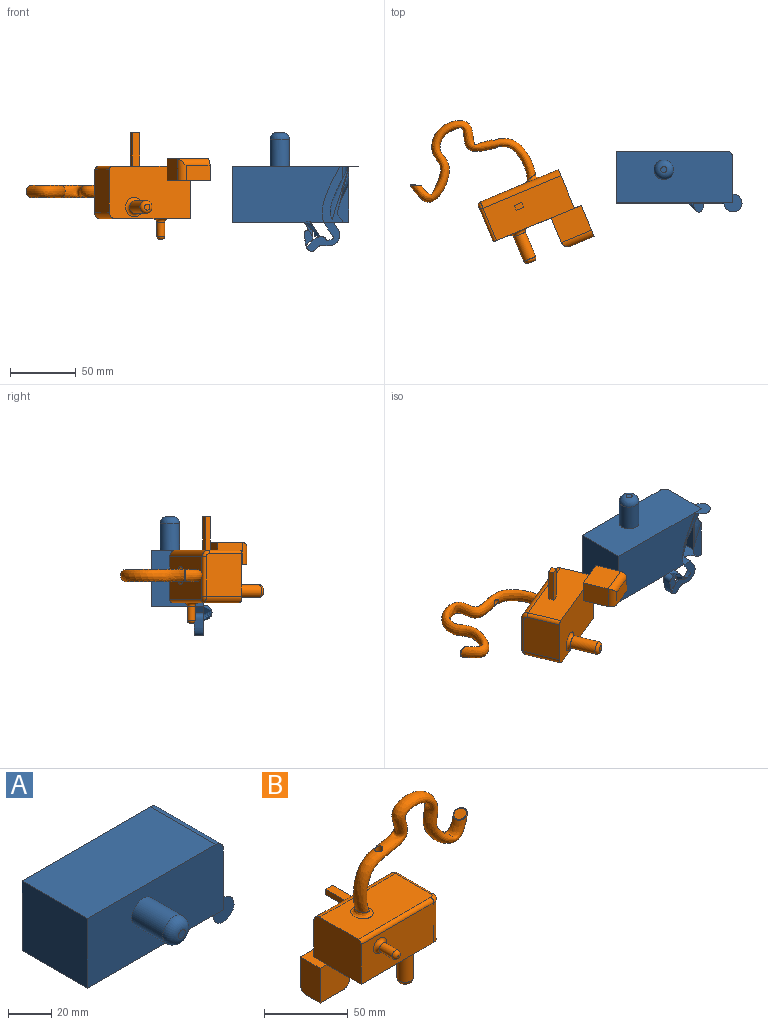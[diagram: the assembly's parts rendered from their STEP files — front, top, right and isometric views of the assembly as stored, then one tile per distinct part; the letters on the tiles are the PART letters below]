
ASSEMBLY  parts=2 mates=1
PART A: 18 faces, bbox 99x100.1x49.5 mm
  f0: plane 88.83x39.37mm, normal (0,1,0), area 3439.5mm2, adj f1,f2,f3,f5,f6,f9,f11,f13
  f1: plane 81.98x42.62mm, normal (0,0,-1), area 3046.3mm2, adj f0,f3,f4,f13,f15
  f2: plane 29.46x8.68mm, normal (0,0,-1), area 162.5mm2, adj f0,f5,f15
  f3: plane 42.61x39.37mm, normal (-1,0,0), area 1677.7mm2, adj f0,f1,f4,f6
  f4: plane 88.83x39.37mm, normal (0,-1,0), area 3320.7mm2, adj f1,f3,f5,f6,f7,f9,f12,f16
  f5: plane 42.61x34.29mm, normal (1,0,0), area 1390.4mm2, adj f0,f2,f4,f9,f15
  f6: plane 83.75x42.61mm, normal (0,0,1), area 3568.8mm2, adj f0,f3,f4,f9
  f7: cylinder r=7.38mm len=20.32mm, axis (0,1,0), area 941.7mm2, adj f4,f10
  f8: plane 4.59x4.59mm, normal (0,-1,0), area 16.6mm2, adj f10
  f9: cylinder r=5.08mm len=42.61mm, axis (0,-1,0), area 340mm2, adj f0,f4,f5,f6
  f10: torus R=2.3mm, axis (0,-1,0), area 277.2mm2, adj f7,f8
  f11: bspline ~26.97x24.13mm, area 437.2mm2, adj f0,f13,f15,f17
  f12: plane 6.86x0.02mm, normal (0,0,1), area 0.2mm2, adj f4,f14,f15,f16
  f13: plane 13.7x11.35mm, normal (0.83,-0.56,0), area 108mm2, adj f0,f1,f11,f15,f17
  f14: plane 13.7x13.7mm, normal (0,-1,0), area 110.5mm2, adj f12,f15,f16
  f15: bspline ~74.52x53.34mm, area 3313.4mm2, adj f0,f1,f2,f5,f11,f12,f13,f14
  f16: bspline ~6.85x0.79mm, area 0.2mm2, adj f4,f12,f14,f15
  f17: plane 27.14x22.5mm, normal (0,0,1), area 299.1mm2, adj f0,f11,f13,f15
PART B: 39 faces, bbox 114.5x81.1x121.9 mm
  f0: bspline ~92.41x72.32mm, area 4159.4mm2, adj f17,f26,f36
  f1: plane 64.11x26.67mm, normal (0,1,0), area 1686.8mm2, adj f2,f6,f11,f12,f13,f14,f16,f23
  f2: plane 39.99x31.75mm, normal (-1,0,0), area 1262.8mm2, adj f1,f3,f5,f6,f16,f23,f29
  f3: plane 61.57x29.21mm, normal (0,-1,0), area 1703mm2, adj f2,f6,f9,f29,f37
  f4: plane 32.37x29.21mm, normal (1,0,0), area 944.2mm2, adj f6,f9,f31,f32,f33
  f5: plane 64.11x32.37mm, normal (0,0,1), area 1935.1mm2, adj f2,f16,f29,f30,f32,f36
  f6: plane 66.65x39.99mm, normal (0,0,-1), area 2278.2mm2, adj f1,f2,f3,f4,f9,f18,f19,f31
  f7: cylinder r=2.98mm len=10.67mm, axis (0,1,0), area 199.5mm2, adj f37,f38
  f8: plane 0.87x0.87mm, normal (0,-1,0), area 0.6mm2, adj f38
  f9: cylinder r=5.08mm len=29.21mm, axis (0,0,1), area 233.1mm2, adj f3,f4,f6,f30
  f10: plane 8.18x6.77mm, normal (-0.5,0,0.87), area 49.9mm2, adj f17
  f11: plane 25.4x3.95mm, normal (1,0,0), area 100.3mm2, adj f1,f12,f14,f15
  f12: plane 25.4x5.84mm, normal (0,0,-1), area 148.4mm2, adj f1,f11,f13,f15
  f13: plane 25.4x3.95mm, normal (-1,0,0), area 100.3mm2, adj f1,f12,f14,f15
  f14: plane 25.4x5.84mm, normal (0,0,1), area 148.4mm2, adj f1,f11,f13,f15
  f15: plane 5.84x3.95mm, normal (0,1,0), area 23.1mm2, adj f11,f12,f13,f14
  f16: cylinder r=5.08mm len=64.11mm, axis (1,0,0), area 511.6mm2, adj f1,f2,f5,f33
  f17: bspline ~9.27x8.04mm, area 21.6mm2, adj f0,f10
  f18: plane 20.32x16.65mm, normal (1,0,0), area 338.3mm2, adj f6,f19,f21,f23,f28
  f19: plane 25.4x24.78mm, normal (0,-1,0), area 623.8mm2, adj f6,f18,f20,f22,f23,f28
  f20: plane 25.4x16.65mm, normal (-1,0,0), area 417.3mm2, adj f19,f21,f22,f23,f27
  f21: plane 24.78x20.32mm, normal (0,1,0), area 503.5mm2, adj f18,f20,f23,f27
  f22: plane 19.7x11.57mm, normal (0,0,-1), area 227.8mm2, adj f19,f20,f27,f28
  f23: plane 24.78x16.65mm, normal (0,0,1), area 203.2mm2, adj f1,f2,f18,f19,f20,f21
  f24: cylinder r=4.84mm len=20.07mm, axis (0,0,1), area 610.6mm2, adj f34,f35
  f25: plane 4.61x4.61mm, normal (0,0,-1), area 16.7mm2, adj f35
  f26: cylinder r=2.54mm len=7.75mm, axis (0,0,-1), area 97.8mm2, adj f0
  f27: cylinder r=5.08mm len=24.78mm, axis (-1,0,0), area 177.4mm2, adj f20,f21,f22,f28
  f28: cylinder r=5.08mm len=16.65mm, axis (0,1,0), area 112.6mm2, adj f18,f19,f22,f27
  f29: cylinder r=2.54mm len=61.57mm, axis (-1,0,0), area 245.7mm2, adj f2,f3,f5,f30
  f30: torus R=2.54mm, axis (0,0,1), area 26.1mm2, adj f5,f9,f29,f32
  f31: cylinder r=2.54mm len=26.67mm, axis (0,0,-1), area 106.4mm2, adj f1,f4,f6,f33
  f32: cylinder r=2.54mm len=29.83mm, axis (0,-1,0), area 119mm2, adj f4,f5,f30,f33
  f33: torus R=2.54mm, axis (1,0,0), area 26.1mm2, adj f4,f16,f31,f32
  f34: torus R=7.38mm, axis (0,0,1), area 144.5mm2, adj f6,f24
  f35: torus R=2.3mm, axis (0,0,1), area 98.3mm2, adj f24,f25
  f36: bspline ~14.28x12.33mm, area 123.1mm2, adj f0,f5
  f37: torus R=5.52mm, axis (0,1,0), area 97.7mm2, adj f3,f7
  f38: torus R=0.44mm, axis (0,-1,0), area 51.5mm2, adj f7,f8
PLACE A rot(axis=(-1,0,0),90deg) t=(-95.35,-22.38,-41.84)mm
PLACE B rot(axis=(0.14,-0.7,-0.7),164.1deg) t=(-196.01,-39.95,-37.11)mm
MATE planar A.f4 <-> B.f1  axis (0,0,1) through (-86.91,-3.01,-17.84)mm
